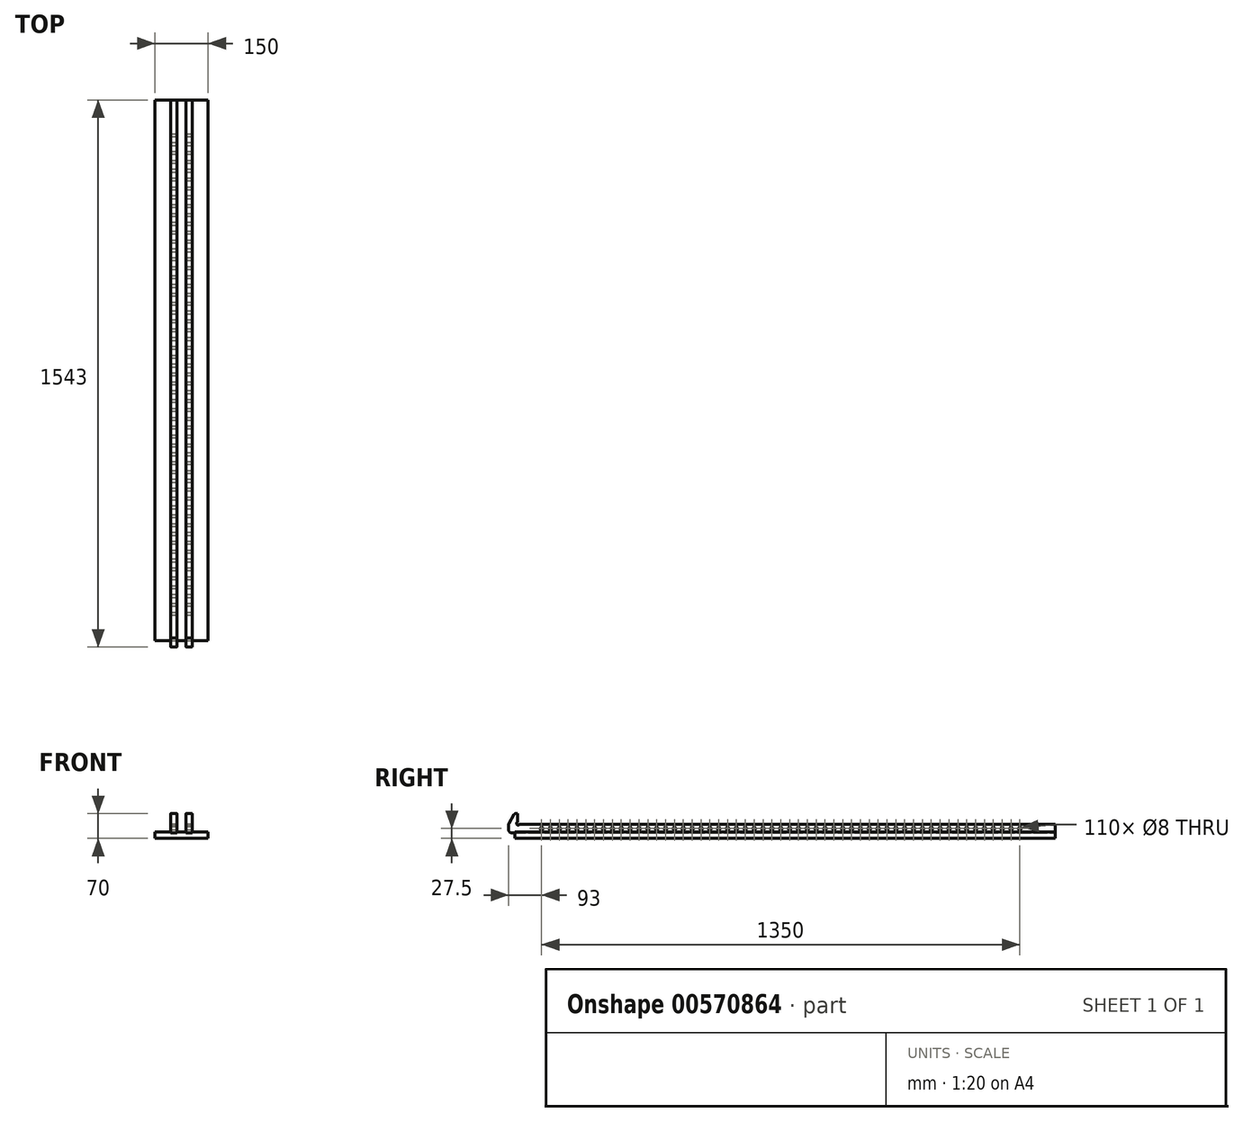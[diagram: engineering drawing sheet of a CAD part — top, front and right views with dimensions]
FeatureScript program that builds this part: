
annotation { "Feature Type Name" : "Feature", "Feature Type Description" : "" }
export const myFeature = defineFeature(function(context is Context, id is Id, definition is map)
    precondition{}
    {
        {
            var Q0;
            Q0=qCreatedBy(makeId("Right.planeOp"),FACE);
            var sketch = newSketch(context, id + "F0", { "sketchPlane" : qUnion([Q0])});
            skLineSegment(sketch, "E0", {"start": v(-18, 70) * mm, "end": v(-23.06, 70) * mm});
            skLineSegment(sketch, "E1", {"start": v(-27.47, 67.45) * mm, "end": v(-42.33, 41.72) * mm});
            skLineSegment(sketch, "E2", {"start": v(-43, 39.22) * mm, "end": v(-43, 25) * mm});
            skLineSegment(sketch, "E3", {"start": v(-33, 15) * mm, "end": v(1500, 15) * mm});
            skLineSegment(sketch, "E4", {"start": v(1500, 15) * mm, "end": v(1500, 40) * mm});
            skLineSegment(sketch, "E5", {"start": v(1500, 40) * mm, "end": v(-9.92, 40) * mm});
            skLineSegment(sketch, "E6", {"start": v(-18, 48.08) * mm, "end": v(-18, 70) * mm});
            skArc(sketch, "E7", {"start": v(-19.44, 44.57) * mm, "mid": v(-19.41, 38.59) * mm, "end": v(-13.43, 38.56) * mm});
            skLineSegment(sketch, "E8", {"start": v(-18, 40) * mm, "end": v(-16.4, 41.6) * mm, "construction": true});
            skPoint(sketch, "E9", {"position": v(-19.41, 38.59) * mm});
            skPoint(sketch, "E10.orphan", {"position": v(-18, 40) * mm});
            skCircle(sketch, "E11", {"center": v(50, 27.5) * mm, "radius": 4 * mm});
            skLineSegment(sketch, "E12", {"start": v(50, 40) * mm, "end": v(50, 15) * mm, "construction": true});
            skCircle(sketch, "E13.1.0.0", {"center": v(75, 27.5) * mm, "radius": 4 * mm});
            skCircle(sketch, "E13.2.0.0", {"center": v(100, 27.5) * mm, "radius": 4 * mm});
            skLineSegment(sketch, "E13.direction1", {"start": v(50, 27.5) * mm, "end": v(75, 27.5) * mm, "construction": true});
            skCircle(sketch, "E14.0.3.0", {"center": v(125, 27.5) * mm, "radius": 4 * mm});
            skCircle(sketch, "E14.0.4.0", {"center": v(150, 27.5) * mm, "radius": 4 * mm});
            skCircle(sketch, "E14.0.5.0", {"center": v(175, 27.5) * mm, "radius": 4 * mm});
            skCircle(sketch, "E14.0.6.0", {"center": v(200, 27.5) * mm, "radius": 4 * mm});
            skCircle(sketch, "E14.0.7.0", {"center": v(225, 27.5) * mm, "radius": 4 * mm});
            skCircle(sketch, "E14.0.8.0", {"center": v(250, 27.5) * mm, "radius": 4 * mm});
            skCircle(sketch, "E14.0.9.0", {"center": v(275, 27.5) * mm, "radius": 4 * mm});
            skCircle(sketch, "E15.0.10.0", {"center": v(300, 27.5) * mm, "radius": 4 * mm});
            skCircle(sketch, "E15.0.11.0", {"center": v(325, 27.5) * mm, "radius": 4 * mm});
            skCircle(sketch, "E15.0.12.0", {"center": v(350, 27.5) * mm, "radius": 4 * mm});
            skCircle(sketch, "E15.0.13.0", {"center": v(375, 27.5) * mm, "radius": 4 * mm});
            skCircle(sketch, "E15.0.14.0", {"center": v(400, 27.5) * mm, "radius": 4 * mm});
            skCircle(sketch, "E15.0.15.0", {"center": v(425, 27.5) * mm, "radius": 4 * mm});
            skCircle(sketch, "E15.0.16.0", {"center": v(450, 27.5) * mm, "radius": 4 * mm});
            skCircle(sketch, "E15.0.17.0", {"center": v(475, 27.5) * mm, "radius": 4 * mm});
            skCircle(sketch, "E15.0.18.0", {"center": v(500, 27.5) * mm, "radius": 4 * mm});
            skCircle(sketch, "E15.0.19.0", {"center": v(525, 27.5) * mm, "radius": 4 * mm});
            skCircle(sketch, "E15.0.20.0", {"center": v(550, 27.5) * mm, "radius": 4 * mm});
            skCircle(sketch, "E15.0.21.0", {"center": v(575, 27.5) * mm, "radius": 4 * mm});
            skCircle(sketch, "E15.0.22.0", {"center": v(600, 27.5) * mm, "radius": 4 * mm});
            skCircle(sketch, "E15.0.23.0", {"center": v(625, 27.5) * mm, "radius": 4 * mm});
            skCircle(sketch, "E15.0.24.0", {"center": v(650, 27.5) * mm, "radius": 4 * mm});
            skCircle(sketch, "E15.0.25.0", {"center": v(675, 27.5) * mm, "radius": 4 * mm});
            skCircle(sketch, "E15.0.26.0", {"center": v(700, 27.5) * mm, "radius": 4 * mm});
            skCircle(sketch, "E15.0.27.0", {"center": v(725, 27.5) * mm, "radius": 4 * mm});
            skCircle(sketch, "E15.0.28.0", {"center": v(750, 27.5) * mm, "radius": 4 * mm});
            skCircle(sketch, "E15.0.29.0", {"center": v(775, 27.5) * mm, "radius": 4 * mm});
            skCircle(sketch, "E16.0.30.0", {"center": v(800, 27.5) * mm, "radius": 4 * mm});
            skCircle(sketch, "E16.0.31.0", {"center": v(825, 27.5) * mm, "radius": 4 * mm});
            skCircle(sketch, "E16.0.32.0", {"center": v(850, 27.5) * mm, "radius": 4 * mm});
            skCircle(sketch, "E16.0.33.0", {"center": v(875, 27.5) * mm, "radius": 4 * mm});
            skCircle(sketch, "E16.0.34.0", {"center": v(900, 27.5) * mm, "radius": 4 * mm});
            skCircle(sketch, "E16.0.35.0", {"center": v(925, 27.5) * mm, "radius": 4 * mm});
            skCircle(sketch, "E16.0.36.0", {"center": v(950, 27.5) * mm, "radius": 4 * mm});
            skCircle(sketch, "E16.0.37.0", {"center": v(975, 27.5) * mm, "radius": 4 * mm});
            skCircle(sketch, "E16.0.38.0", {"center": v(1000, 27.5) * mm, "radius": 4 * mm});
            skCircle(sketch, "E16.0.39.0", {"center": v(1025, 27.5) * mm, "radius": 4 * mm});
            skCircle(sketch, "E16.0.40.0", {"center": v(1050, 27.5) * mm, "radius": 4 * mm});
            skCircle(sketch, "E16.0.41.0", {"center": v(1075, 27.5) * mm, "radius": 4 * mm});
            skCircle(sketch, "E16.0.42.0", {"center": v(1100, 27.5) * mm, "radius": 4 * mm});
            skCircle(sketch, "E16.0.43.0", {"center": v(1125, 27.5) * mm, "radius": 4 * mm});
            skCircle(sketch, "E16.0.44.0", {"center": v(1150, 27.5) * mm, "radius": 4 * mm});
            skCircle(sketch, "E16.0.45.0", {"center": v(1175, 27.5) * mm, "radius": 4 * mm});
            skCircle(sketch, "E16.0.46.0", {"center": v(1200, 27.5) * mm, "radius": 4 * mm});
            skCircle(sketch, "E16.0.47.0", {"center": v(1225, 27.5) * mm, "radius": 4 * mm});
            skCircle(sketch, "E16.0.48.0", {"center": v(1250, 27.5) * mm, "radius": 4 * mm});
            skCircle(sketch, "E16.0.49.0", {"center": v(1275, 27.5) * mm, "radius": 4 * mm});
            skCircle(sketch, "E17.0.50.0", {"center": v(1300, 27.5) * mm, "radius": 4 * mm});
            skCircle(sketch, "E17.0.51.0", {"center": v(1325, 27.5) * mm, "radius": 4 * mm});
            skCircle(sketch, "E17.0.52.0", {"center": v(1350, 27.5) * mm, "radius": 4 * mm});
            skCircle(sketch, "E17.0.53.0", {"center": v(1375, 27.5) * mm, "radius": 4 * mm});
            skCircle(sketch, "E17.0.54.0", {"center": v(1400, 27.5) * mm, "radius": 4 * mm});
            skPoint(sketch, "E18.visualSharp", {"position": v(-43, 15) * mm});
            skArc(sketch, "E18.filletArc", {"start": v(-43, 25) * mm, "mid": v(-40.07, 17.93) * mm, "end": v(-33, 15) * mm});
            skPoint(sketch, "E19.visualSharp", {"position": v(-43, 40.56) * mm});
            skArc(sketch, "E19.filletArc", {"start": v(-42.33, 41.72) * mm, "mid": v(-42.83, 40.5) * mm, "end": v(-43, 39.22) * mm});
            skPoint(sketch, "E20.visualSharp", {"position": v(-26, 70) * mm});
            skArc(sketch, "E20.filletArc", {"start": v(-23.06, 70) * mm, "mid": v(-25.6, 69.32) * mm, "end": v(-27.47, 67.45) * mm});
            skPoint(sketch, "E21.visualSharp", {"position": v(-18, 45.53) * mm});
            skArc(sketch, "E21.filletArc", {"start": v(-19.44, 44.57) * mm, "mid": v(-18.37, 46.19) * mm, "end": v(-18, 48.08) * mm});
            skPoint(sketch, "E22.visualSharp", {"position": v(-12.47, 40) * mm});
            skArc(sketch, "E22.filletArc", {"start": v(-9.92, 40) * mm, "mid": v(-11.81, 39.63) * mm, "end": v(-13.43, 38.56) * mm});
            skSolve(sketch);
        }
        {
            var Q0;
            Q0=makeQuery(id+"F0.imprint","IMPRINT",FACE,{"disambiguationData":[TD([[makeQuery(id+"F0.imprint","IMPRINT",EDGE,{"derivedFrom":sQuery(id+"F0.wireOp",EDGE,"E0")}),1.0]])]});
            extrude(context, id + "F1", {"entities" : qUnion([Q0]), "depth" : 18 * mm, "offsetDistance" : 25 * mm});
        }
        {
            var Q0;
            Q0=makeQuery(id+"F1.opExtrude","SWEPT_BODY",BODY,{"disambiguationData":[OSD([sQuery(id+"F0.wireOp",EDGE,"E0"),sQuery(id+"F0.wireOp",EDGE,"E1"),sQuery(id+"F0.wireOp",EDGE,"E2"),sQuery(id+"F0.wireOp",EDGE,"E3"),sQuery(id+"F0.wireOp",EDGE,"E4"),sQuery(id+"F0.wireOp",EDGE,"E5"),sQuery(id+"F0.wireOp",EDGE,"E6"),sQuery(id+"F0.wireOp",EDGE,"E7"),sQuery(id+"F0.wireOp",EDGE,"E11"),sQuery(id+"F0.wireOp",EDGE,"E13.1.0.0"),sQuery(id+"F0.wireOp",EDGE,"E13.2.0.0"),sQuery(id+"F0.wireOp",EDGE,"E14.0.3.0"),sQuery(id+"F0.wireOp",EDGE,"E14.0.4.0"),sQuery(id+"F0.wireOp",EDGE,"E14.0.5.0"),sQuery(id+"F0.wireOp",EDGE,"E14.0.6.0"),sQuery(id+"F0.wireOp",EDGE,"E14.0.7.0"),sQuery(id+"F0.wireOp",EDGE,"E14.0.8.0"),sQuery(id+"F0.wireOp",EDGE,"E14.0.9.0"),sQuery(id+"F0.wireOp",EDGE,"E15.0.10.0"),sQuery(id+"F0.wireOp",EDGE,"E15.0.11.0"),sQuery(id+"F0.wireOp",EDGE,"E15.0.12.0"),sQuery(id+"F0.wireOp",EDGE,"E15.0.13.0"),sQuery(id+"F0.wireOp",EDGE,"E15.0.14.0"),sQuery(id+"F0.wireOp",EDGE,"E15.0.15.0"),sQuery(id+"F0.wireOp",EDGE,"E15.0.16.0"),sQuery(id+"F0.wireOp",EDGE,"E15.0.17.0"),sQuery(id+"F0.wireOp",EDGE,"E15.0.18.0"),sQuery(id+"F0.wireOp",EDGE,"E15.0.19.0"),sQuery(id+"F0.wireOp",EDGE,"E15.0.20.0"),sQuery(id+"F0.wireOp",EDGE,"E15.0.21.0"),sQuery(id+"F0.wireOp",EDGE,"E15.0.22.0"),sQuery(id+"F0.wireOp",EDGE,"E15.0.23.0"),sQuery(id+"F0.wireOp",EDGE,"E15.0.24.0"),sQuery(id+"F0.wireOp",EDGE,"E15.0.25.0"),sQuery(id+"F0.wireOp",EDGE,"E15.0.26.0"),sQuery(id+"F0.wireOp",EDGE,"E15.0.27.0"),sQuery(id+"F0.wireOp",EDGE,"E15.0.28.0"),sQuery(id+"F0.wireOp",EDGE,"E15.0.29.0"),sQuery(id+"F0.wireOp",EDGE,"E16.0.30.0"),sQuery(id+"F0.wireOp",EDGE,"E16.0.31.0"),sQuery(id+"F0.wireOp",EDGE,"E16.0.32.0"),sQuery(id+"F0.wireOp",EDGE,"E16.0.33.0"),sQuery(id+"F0.wireOp",EDGE,"E16.0.34.0"),sQuery(id+"F0.wireOp",EDGE,"E16.0.35.0"),sQuery(id+"F0.wireOp",EDGE,"E16.0.36.0"),sQuery(id+"F0.wireOp",EDGE,"E16.0.37.0"),sQuery(id+"F0.wireOp",EDGE,"E16.0.38.0"),sQuery(id+"F0.wireOp",EDGE,"E16.0.39.0"),sQuery(id+"F0.wireOp",EDGE,"E16.0.40.0"),sQuery(id+"F0.wireOp",EDGE,"E16.0.41.0"),sQuery(id+"F0.wireOp",EDGE,"E16.0.42.0"),sQuery(id+"F0.wireOp",EDGE,"E16.0.43.0"),sQuery(id+"F0.wireOp",EDGE,"E16.0.44.0"),sQuery(id+"F0.wireOp",EDGE,"E16.0.45.0"),sQuery(id+"F0.wireOp",EDGE,"E16.0.46.0"),sQuery(id+"F0.wireOp",EDGE,"E16.0.47.0"),sQuery(id+"F0.wireOp",EDGE,"E16.0.48.0"),sQuery(id+"F0.wireOp",EDGE,"E16.0.49.0"),sQuery(id+"F0.wireOp",EDGE,"E17.0.50.0"),sQuery(id+"F0.wireOp",EDGE,"E17.0.51.0"),sQuery(id+"F0.wireOp",EDGE,"E17.0.52.0"),sQuery(id+"F0.wireOp",EDGE,"E17.0.53.0"),sQuery(id+"F0.wireOp",EDGE,"E17.0.54.0"),sQuery(id+"F0.wireOp",EDGE,"E18.filletArc"),sQuery(id+"F0.wireOp",EDGE,"E19.filletArc"),sQuery(id+"F0.wireOp",EDGE,"E20.filletArc"),sQuery(id+"F0.wireOp",EDGE,"E21.filletArc"),sQuery(id+"F0.wireOp",EDGE,"E22.filletArc")])]});
            transform(context, id + "F2", {"entities" : qUnion([Q0]), "transformType" : TransformType.TRANSLATION_3D, "dx" : 43 * mm, "dy" : 0 * mm, "dz" : 0 * mm, "makeCopy" : true});
        }
        {
            var Q0;
            Q0=qCreatedBy(makeId("Front.planeOp"),FACE);
            var sketch = newSketch(context, id + "F3", { "sketchPlane" : qUnion([Q0])});
            skLineSegment(sketch, "E23.bottom", {"start": v(-44.25, 0) * mm, "end": v(105.75, 0) * mm});
            skLineSegment(sketch, "E23.top", {"start": v(-44.25, 18) * mm, "end": v(-0.25, 18) * mm});
            skLineSegment(sketch, "E23.left", {"start": v(-44.25, 0) * mm, "end": v(-44.25, 18) * mm});
            skLineSegment(sketch, "E23.right", {"start": v(105.75, 0) * mm, "end": v(105.75, 18) * mm});
            skLineSegment(sketch, "E24.top", {"start": v(-0.25, 15) * mm, "end": v(18.25, 15) * mm});
            skLineSegment(sketch, "E24.left", {"start": v(-0.25, 18) * mm, "end": v(-0.25, 15) * mm});
            skLineSegment(sketch, "E24.right", {"start": v(18.25, 18) * mm, "end": v(18.25, 15) * mm});
            skLineSegment(sketch, "E25.top", {"start": v(43.25, 15) * mm, "end": v(61.75, 15) * mm});
            skLineSegment(sketch, "E25.left", {"start": v(43.25, 18) * mm, "end": v(43.25, 15) * mm});
            skLineSegment(sketch, "E26.trimOffspring", {"start": v(18.25, 18) * mm, "end": v(43.25, 18) * mm});
            skLineSegment(sketch, "E27", {"start": v(61.75, 15) * mm, "end": v(61.75, 18) * mm});
            skLineSegment(sketch, "E28", {"start": v(105.75, 18) * mm, "end": v(61.75, 18) * mm});
            skSolve(sketch);
        }
        {
            var Q0;
            Q0=makeQuery(id+"F3.imprint","IMPRINT",FACE,{"disambiguationData":[TD([[makeQuery(id+"F3.imprint","IMPRINT",EDGE,{"derivedFrom":sQuery(id+"F3.wireOp",EDGE,"E23.bottom")}),1.0]])]});
            extrude(context, id + "F4", {"entities" : qUnion([Q0]), "depth" : 25 * mm, "offsetDistance" : 25 * mm, "hasSecondDirection" : true, "secondDirectionOppositeDirection" : true, "secondDirectionDepth" : 1500 * mm});
        }
    });
